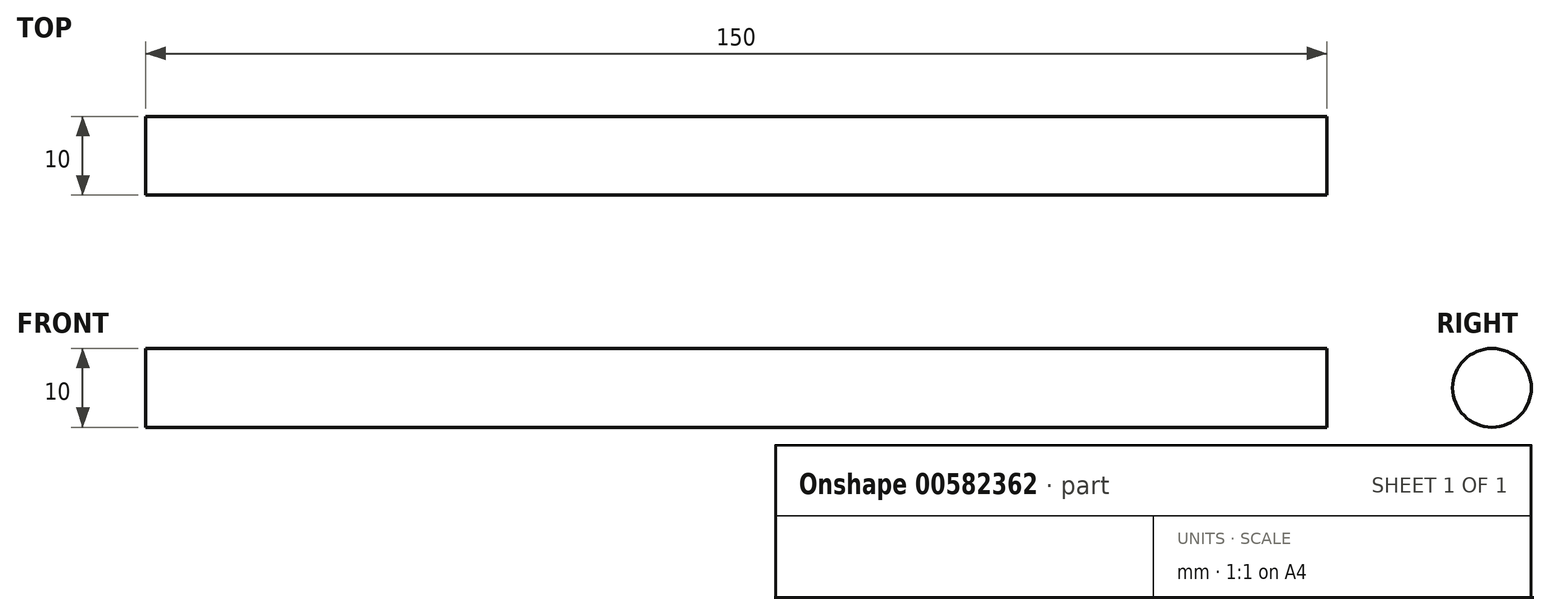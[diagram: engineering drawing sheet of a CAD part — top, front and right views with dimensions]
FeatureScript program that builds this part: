
annotation { "Feature Type Name" : "Feature", "Feature Type Description" : "" }
export const myFeature = defineFeature(function(context is Context, id is Id, definition is map)
    precondition{}
    {
        {
            var Q0;
            Q0=qCreatedBy(makeId("Right.planeOp"),FACE);
            var sketch = newSketch(context, id + "F0", { "sketchPlane" : qUnion([Q0])});
            skCircle(sketch, "E0", {"center": v(0, 0) * mm, "radius": 5 * mm});
            skSolve(sketch);
        }
        {
            var Q0;
            Q0 = qSketchRegion(id + "F0", true);
            var Q1;
            Q1 = qConstructionFilter(qBodyType(qCreatedBy(id + "F0" ,EDGE), BodyType.WIRE), ConstructionObject.NO);
            extrude(context, id + "F1", {"entities" : qUnion([Q0]), "surfaceEntities" : qUnion([Q1]), "depth" : 150 * mm, "offsetDistance" : 25 * mm});
        }
    });
